# Revit family: D30
name_source: partatom
category: Plumbing Fixtures
revit_build: Autodesk Revit 2016 (Build: 20190508_0715(x64)
units: mm (PartAtom-declared; Revit-internal decimal feet)

## family parameters
Always vertical = Yes
Cut with Voids When Loaded = No
OmniClass Number = 23.45.00.00
OmniClass Title = Sanitary, Laundry, and Cleaning Equipment
Part Type = Normal
Room Calculation Point = No
Round Connector Dimension = Use Diameter
Shared = No
Work Plane-Based = No

## types (6) — shared parameters
A2 = 306 mm  [stored 1.00394 ft]
Aluminium = Aluminum - Polished
Chrome = Chrome
Glass = Glass
H = 2000 mm  [stored 6.56168 ft]
Manufacturer = SanSwiss
Model = D30
Seal = Seal
URL = www.sanswiss.com

## per-type parameters (varying)
| type | A | A1 | B |
| 900x900 | 900 mm  [stored 2.95276 ft] | 594 mm | 900 mm  [stored 2.95276 ft] |
| 700x800 | 700 mm  [stored 2.29659 ft] | 394 mm | 800 mm  [stored 2.62467 ft] |
| 750x900 | 750 mm  [stored 2.46063 ft] | 444 mm | 900 mm  [stored 2.95276 ft] |
| 800x900 | 800 mm  [stored 2.62467 ft] | 494 mm | 900 mm  [stored 2.95276 ft] |
| 800x1000 | 800 mm  [stored 2.62467 ft] | 494 mm | 1000 mm  [stored 3.28084 ft] |
| 900x1000 | 900 mm  [stored 2.95276 ft] | 594 mm | 1000 mm  [stored 3.28084 ft] |

note: [stored X ft] marks values corroborated as IEEE doubles in the binary element streams (Revit-internal decimal feet)

## geometry (parser evidence)
native form markers: Sweep x12
no freeform markers — native parametric forms only
